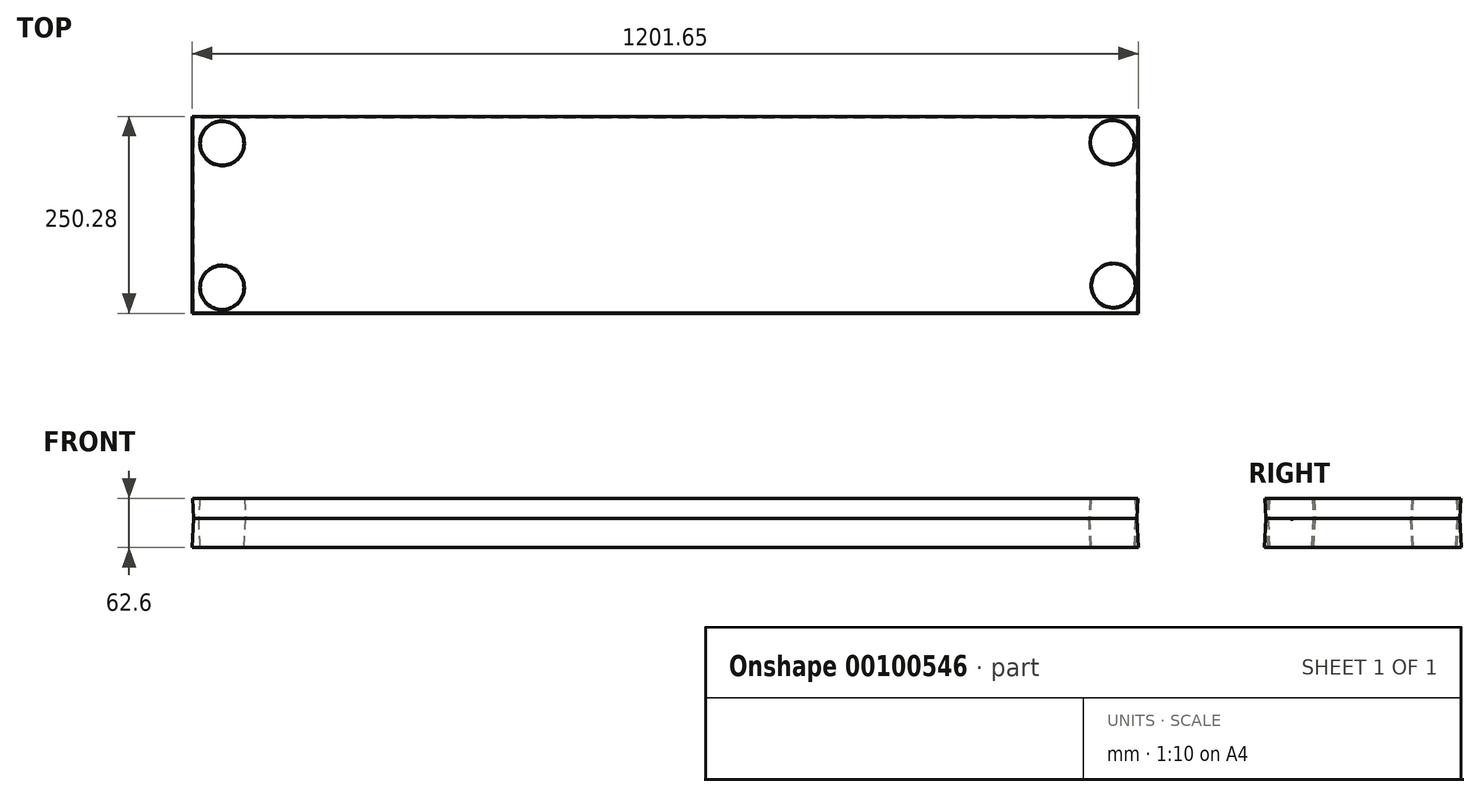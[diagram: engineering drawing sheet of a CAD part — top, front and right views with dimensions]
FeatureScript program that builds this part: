
annotation { "Feature Type Name" : "Feature", "Feature Type Description" : "" }
export const myFeature = defineFeature(function(context is Context, id is Id, definition is map)
    precondition{}
    {
        {
            var Q0;
            Q0=qCreatedBy(makeId("Front.planeOp"),FACE);
            var sketch = newSketch(context, id + "F0", { "sketchPlane" : qUnion([Q0])});
            skLineSegment(sketch, "E0.bottom", {"start": v(-72.95, 18.67) * mm, "end": v(83.4, 18.67) * mm});
            skLineSegment(sketch, "E0.top", {"start": v(-72.95, 5.9) * mm, "end": v(83.4, 5.9) * mm});
            skLineSegment(sketch, "E0.left", {"start": v(-72.95, 18.67) * mm, "end": v(-72.95, 5.9) * mm});
            skLineSegment(sketch, "E0.right", {"start": v(83.4, 18.67) * mm, "end": v(83.4, 5.9) * mm});
            skSolve(sketch);
        }
        {
            var Q0;
            Q0=makeQuery(id+"F0.imprint","IMPRINT",FACE,{"disambiguationData":[TD([[makeQuery(id+"F0.imprint","IMPRINT",EDGE,{"derivedFrom":sQuery(id+"F0.wireOp",EDGE,"E0.bottom")}),-1.0]])]});
            extrude(context, id + "F1", {"entities" : qUnion([Q0]), "depth" : 246.38 * mm});
        }
        {
            var Q0;
            Q0=makeQuery(id+"F1.opExtrude","SWEPT_FACE",FACE,{"disambiguationData":[OSD([sQuery(id+"F0.wireOp",EDGE,"E0.left")])]});
            extrude(context, id + "F2", {"entities" : qUnion([Q0]), "operationType" : NewBodyOperationType.ADD, "depth" : 1041.4 * mm});
        }
        {
            var Q0;
            {var subQ0=sQuery(id+"F0.wireOp",EDGE,"E0.top");Q0=makeQuery(id+"F2.boolean.opBoolean","MERGE",FACE,{"derivedFrom":[makeQuery(id+"F1.opExtrude","SWEPT_FACE",FACE,{"disambiguationData":[OSD([subQ0])]}),makeQuery(id+"F2.opExtrude","SWEPT_FACE",FACE,{"disambiguationData":[OSD([subQ0,sQuery(id+"F0.wireOp",EDGE,"E0.left")])]})]});}
            var sketch = newSketch(context, id + "F3", { "sketchPlane" : qUnion([Q0])});
            skSolve(sketch);
        }
        {
            var Q0;
            {var subQ0=sQuery(id+"F0.wireOp",EDGE,"E0.top");Q0=makeQuery(id+"F3.imprint","IMPRINT",FACE,{"disambiguationData":[TD([[makeQuery(id+"F3.imprint","IMPRINT",EDGE,{"derivedFrom":makeQuery(id+"F1.opExtrude","SWEPT_EDGE",EDGE,{"disambiguationData":[OSD([subQ0,sQuery(id+"F0.wireOp",EDGE,"E0.right")])]})}),-1.0]])]});}
            var sketch = newSketch(context, id + "F4", { "sketchPlane" : qUnion([Q0])});
            skLineSegment(sketch, "E1", {"start": v(-1116.03, 129.6) * mm, "end": v(82.34, 129.6) * mm});
            skSolve(sketch);
        }
        {
            var Q0;
            {var subQ0=sQuery(id+"F0.wireOp",EDGE,"E0.top");Q0=makeQuery(id+"F3.imprint","IMPRINT",FACE,{"disambiguationData":[TD([[makeQuery(id+"F3.imprint","IMPRINT",EDGE,{"derivedFrom":makeQuery(id+"F1.opExtrude","SWEPT_EDGE",EDGE,{"disambiguationData":[OSD([subQ0,sQuery(id+"F0.wireOp",EDGE,"E0.right")])]})}),-1.0]])]});}
            var sketch = newSketch(context, id + "F5", { "sketchPlane" : qUnion([Q0])});
            skLineSegment(sketch, "E2.0", {"start": v(-1116.03, 114.76) * mm, "end": v(82.34, 114.76) * mm});
            skSolve(sketch);
        }
        {
            var Q0;
            {var subQ0=sQuery(id+"F0.wireOp",EDGE,"E0.top");Q0=makeQuery(id+"F5.imprint","IMPRINT",FACE,{"disambiguationData":[TD([[makeQuery(id+"F5.imprint","IMPRINT",EDGE,{"derivedFrom":makeQuery(id+"F3.imprint","IMPRINT",EDGE,{"derivedFrom":makeQuery(id+"F1.opExtrude","SWEPT_EDGE",EDGE,{"disambiguationData":[OSD([subQ0,sQuery(id+"F0.wireOp",EDGE,"E0.right")])]})})}),-1.0]])]});}
            var sketch = newSketch(context, id + "F6", { "sketchPlane" : qUnion([Q0])});
            skLineSegment(sketch, "E3.bottom", {"start": v(-1107.71, 245.18) * mm, "end": v(-1046.67, 245.18) * mm});
            skLineSegment(sketch, "E3.top", {"start": v(-1107.71, 184.14) * mm, "end": v(-1046.67, 184.14) * mm});
            skLineSegment(sketch, "E3.left", {"start": v(-1107.71, 245.18) * mm, "end": v(-1107.71, 184.14) * mm});
            skLineSegment(sketch, "E3.right", {"start": v(-1046.67, 245.18) * mm, "end": v(-1046.67, 184.14) * mm});
            skLineSegment(sketch, "E4.bottom", {"start": v(-1107.71, 0) * mm, "end": v(-1046.67, 0) * mm});
            skLineSegment(sketch, "E4.top", {"start": v(-1107.71, 62.05) * mm, "end": v(-1046.67, 62.05) * mm});
            skLineSegment(sketch, "E4.left", {"start": v(-1107.71, 0) * mm, "end": v(-1107.71, 62.05) * mm});
            skLineSegment(sketch, "E4.right", {"start": v(-1046.67, 0) * mm, "end": v(-1046.67, 62.05) * mm});
            skSolve(sketch);
        }
        {
            var Q0;
            {var subQ0=sQuery(id+"F0.wireOp",EDGE,"E0.top");Q0=makeQuery(id+"F5.imprint","IMPRINT",FACE,{"disambiguationData":[TD([[makeQuery(id+"F5.imprint","IMPRINT",EDGE,{"derivedFrom":makeQuery(id+"F3.imprint","IMPRINT",EDGE,{"derivedFrom":makeQuery(id+"F1.opExtrude","SWEPT_EDGE",EDGE,{"disambiguationData":[OSD([subQ0,sQuery(id+"F0.wireOp",EDGE,"E0.right")])]})})}),-1.0]])]});}
            var sketch = newSketch(context, id + "F7", { "sketchPlane" : qUnion([Q0])});
            skLineSegment(sketch, "E5.bottom", {"start": v(81.33, 241.89) * mm, "end": v(20.79, 241.89) * mm});
            skLineSegment(sketch, "E5.top", {"start": v(81.33, 181.34) * mm, "end": v(20.79, 181.34) * mm});
            skLineSegment(sketch, "E5.left", {"start": v(81.33, 241.89) * mm, "end": v(81.33, 181.34) * mm});
            skLineSegment(sketch, "E5.right", {"start": v(20.79, 241.89) * mm, "end": v(20.79, 181.34) * mm});
            skLineSegment(sketch, "E6.bottom", {"start": v(81.33, 0) * mm, "end": v(20.79, 0) * mm});
            skLineSegment(sketch, "E6.top", {"start": v(81.33, 61.54) * mm, "end": v(20.79, 61.54) * mm});
            skLineSegment(sketch, "E6.left", {"start": v(81.33, 0) * mm, "end": v(81.33, 61.54) * mm});
            skLineSegment(sketch, "E6.right", {"start": v(20.79, 0) * mm, "end": v(20.79, 61.54) * mm});
            skSolve(sketch);
        }
        {
            var Q0;
            {var subQ0=sQuery(id+"F0.wireOp",EDGE,"E0.top");Q0=makeQuery(id+"F5.imprint","IMPRINT",FACE,{"disambiguationData":[TD([[makeQuery(id+"F5.imprint","IMPRINT",EDGE,{"derivedFrom":makeQuery(id+"F3.imprint","IMPRINT",EDGE,{"derivedFrom":makeQuery(id+"F1.opExtrude","SWEPT_EDGE",EDGE,{"disambiguationData":[OSD([subQ0,sQuery(id+"F0.wireOp",EDGE,"E0.right")])]})})}),-1.0]])]});}
            var sketch = newSketch(context, id + "F8", { "sketchPlane" : qUnion([Q0])});
            skCircle(sketch, "E7", {"center": v(-1078.37, 215.67) * mm, "radius": 29.9 * mm});
            skCircle(sketch, "E8", {"center": v(-1078.37, 32.43) * mm, "radius": 30.8 * mm});
            skCircle(sketch, "E9", {"center": v(52.53, 31.12) * mm, "radius": 29.68 * mm});
            skCircle(sketch, "E10", {"center": v(53.84, 213.06) * mm, "radius": 29.62 * mm});
            skSolve(sketch);
        }
        {
            var Q0;
            Q0=sQuery(id+"F8.wireOp",VERTEX,"E7.center");
            var Q1;
            Q1=sQuery(id+"F8.wireOp",VERTEX,"E8.center");
            var Q2;
            Q2=sQuery(id+"F8.wireOp",VERTEX,"E9.center");
            var Q3;
            Q3=sQuery(id+"F8.wireOp",VERTEX,"E10.center");
            var Q4;
            Q4=makeQuery(id+"F1.opExtrude","SWEPT_BODY",BODY,{"disambiguationData":[OSD([sQuery(id+"F0.wireOp",EDGE,"E0.bottom"),sQuery(id+"F0.wireOp",EDGE,"E0.top"),sQuery(id+"F0.wireOp",EDGE,"E0.left"),sQuery(id+"F0.wireOp",EDGE,"E0.right")])]});
            hole(context, id + "F9", {"style" : HoleStyle.SIMPLE, "endStyle" : HoleEndStyle.THROUGH, "holeDiameter" : 59.36 * mm, "locations" : qUnion([Q0, Q1, Q2, Q3]), "scope" : qUnion([Q4]), "isTappedThrough" : true});
        }
        {
            var Q0;
            {var subQ0=sQuery(id+"F0.wireOp",EDGE,"E0.top");Q0=makeQuery(id+"F2.boolean.opBoolean","MERGE",FACE,{"derivedFrom":[makeQuery(id+"F1.opExtrude","SWEPT_FACE",FACE,{"disambiguationData":[OSD([subQ0])]}),makeQuery(id+"F2.opExtrude","SWEPT_FACE",FACE,{"disambiguationData":[OSD([subQ0,sQuery(id+"F0.wireOp",EDGE,"E0.left")])]})]});}
            extrude(context, id + "F10", {"entities" : qUnion([Q0]), "operationType" : NewBodyOperationType.ADD, "depth" : 37.2 * mm, "hasDraft" : true, "draftAngle" : 3 * degree, "hasSecondDirection" : true, "secondDirectionOppositeDirection" : true, "secondDirectionDepth" : 25.4 * mm, "hasSecondDirectionDraft" : true, "secondDirectionDraftAngle" : 3 * degree});
        }
    });
